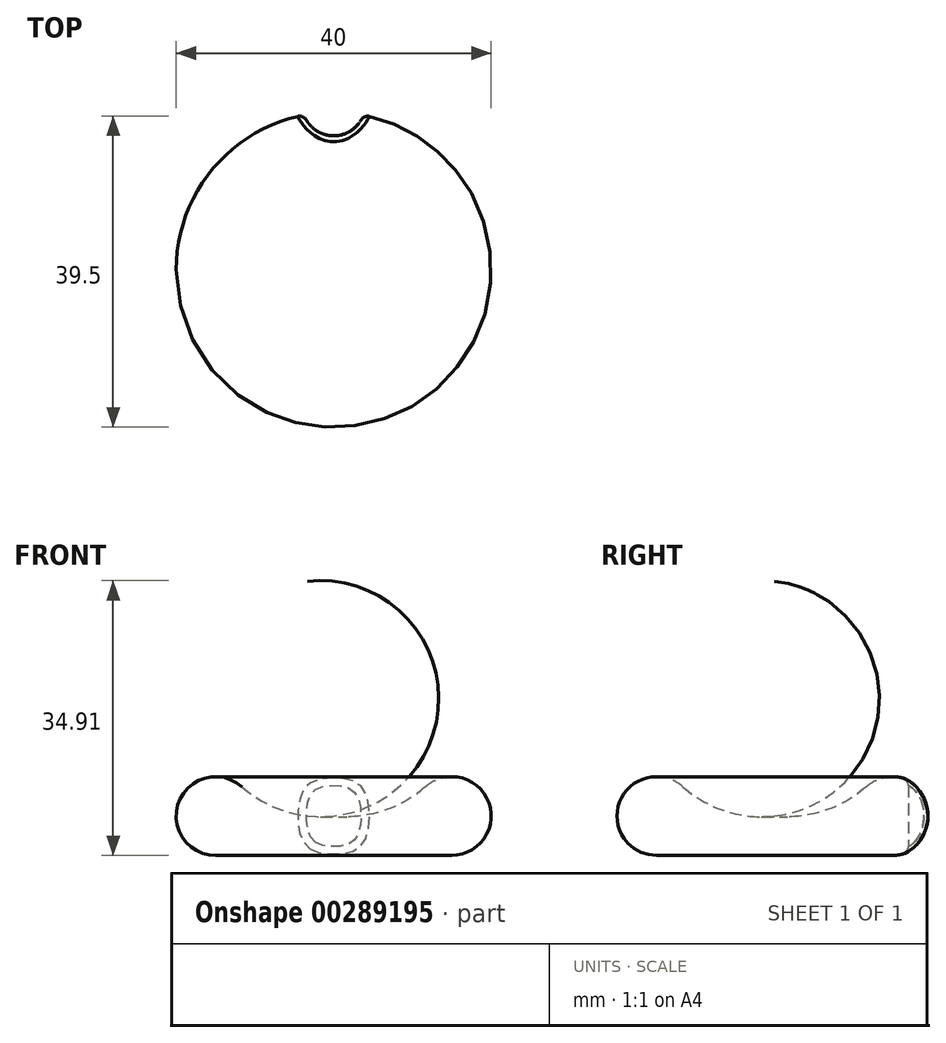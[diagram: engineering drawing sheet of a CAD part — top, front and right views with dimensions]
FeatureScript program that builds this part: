
annotation { "Feature Type Name" : "Feature", "Feature Type Description" : "" }
export const myFeature = defineFeature(function(context is Context, id is Id, definition is map)
    precondition{}
    {
        {
            var Q0;
            Q0=qCreatedBy(makeId("Front.planeOp"),FACE);
            var sketch = newSketch(context, id + "F0", { "sketchPlane" : qUnion([Q0])});
            skArc(sketch, "E0", {"start": v(-56.68, 8.73) * mm, "mid": v(-51.25, 5.62) * mm, "end": v(-45.02, 5) * mm});
            skArc(sketch, "E1", {"start": v(-56.68, 8.73) * mm, "mid": v(-64.69, 6.78) * mm, "end": v(-60.02, 0) * mm});
            skLineSegment(sketch, "E2", {"start": v(-60.02, 0) * mm, "end": v(-45.02, 0) * mm});
            skLineSegment(sketch, "E3", {"start": v(-45.02, 0) * mm, "end": v(-45.02, 5) * mm});
            skSolve(sketch);
        }
        {
            var Q0;
            Q0=makeQuery(id+"F0.imprint","IMPRINT",FACE,{"disambiguationData":[TD([[makeQuery(id+"F0.imprint","IMPRINT",EDGE,{"derivedFrom":sQuery(id+"F0.wireOp",EDGE,"E0")}),-1.0]])]});
            var Q1;
            Q1=sQuery(id+"F0.wireOp",EDGE,"E3");
            revolve(context, id + "F1", {"entities" : qUnion([Q0]), "axis" : qUnion([Q1]), "revolveType" : RevolveType.FULL});
        }
        {
            var Q0;
            Q0=qCreatedBy(makeId("Top.planeOp"),FACE);
            var sketch = newSketch(context, id + "F2", { "sketchPlane" : qUnion([Q0])});
            skCircle(sketch, "E4", {"center": v(-45.02, 21) * mm, "radius": 4 * mm});
            skSolve(sketch);
        }
        {
            var Q0;
            Q0=makeQuery(id+"F2.imprint","IMPRINT",FACE,{"disambiguationData":[TD([[makeQuery(id+"F2.imprint","IMPRINT",EDGE,{"derivedFrom":sQuery(id+"F2.wireOp",EDGE,"E4")}),1.0]])]});
            var Q1;
            Q1=makeQuery(id+"F1.opRevolve","SWEPT_FACE",FACE,{"disambiguationData":[OSD([sQuery(id+"F0.wireOp",EDGE,"E1")])]});
            extrude(context, id + "F3", {"entities" : qUnion([Q0]), "operationType" : NewBodyOperationType.REMOVE, "endBound" : BoundingType.THROUGH_ALL, "endBoundEntityFace" : qUnion([Q1]), "depth" : 25 * mm});
        }
        {
            var Q0;
            Q0=makeQuery(id+"F3.boolean.opBoolean","INTERSECT",EDGE,{"derivedFrom":[makeQuery(id+"F1.opRevolve","SWEPT_FACE",FACE,{"disambiguationData":[OSD([sQuery(id+"F0.wireOp",EDGE,"E1")])]}),makeQuery(id+"F3.opExtrude","SWEPT_FACE",FACE,{"disambiguationData":[OSD([sQuery(id+"F2.wireOp",EDGE,"E4")])]})]});
            fillet(context, id + "F4", {"entities" : qUnion([Q0]), "radius" : 1 * mm, "tangentPropagation" : true, "allowEdgeOverflow" : false});
        }
    });
